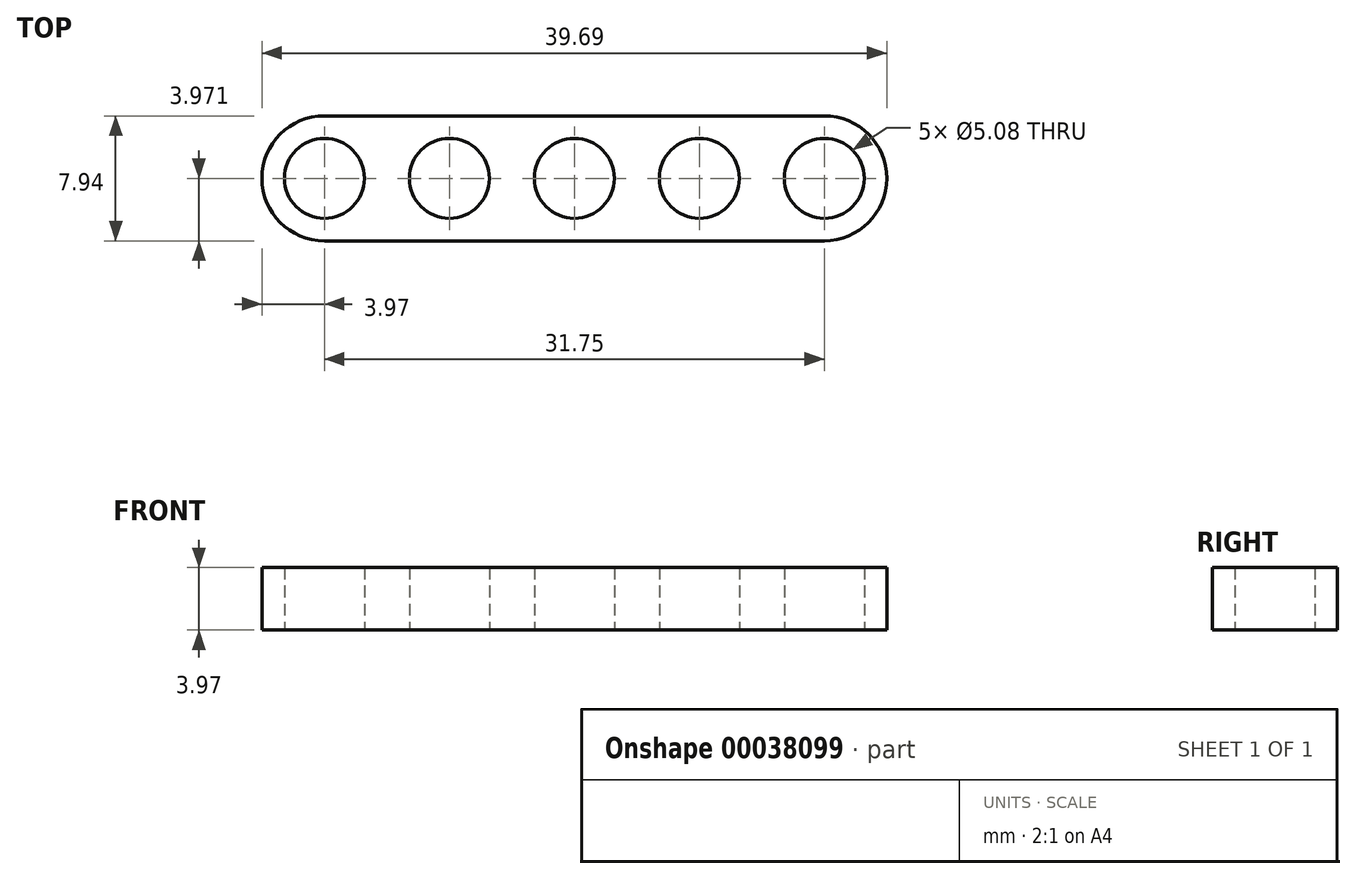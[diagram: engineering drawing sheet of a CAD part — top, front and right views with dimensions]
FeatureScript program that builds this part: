
annotation { "Feature Type Name" : "Feature", "Feature Type Description" : "" }
export const myFeature = defineFeature(function(context is Context, id is Id, definition is map)
    precondition{}
    {
        {
            var Q0;
            Q0=qCreatedBy(makeId("Top.planeOp"),FACE);
            var sketch = newSketch(context, id + "F0", { "sketchPlane" : qUnion([Q0])});
            skLineSegment(sketch, "E0.bottom", {"start": v(0, 0) * mm, "end": v(31.75, 0) * mm});
            skLineSegment(sketch, "E0.top", {"start": v(0, -7.94) * mm, "end": v(31.75, -7.94) * mm});
            skLineSegment(sketch, "E0.left", {"start": v(0, 0) * mm, "end": v(0, -7.94) * mm});
            skLineSegment(sketch, "E0.right", {"start": v(31.75, 0) * mm, "end": v(31.75, -7.94) * mm});
            skLineSegment(sketch, "E1", {"start": v(0, -3.97) * mm, "end": v(7.94, -3.97) * mm, "construction": true});
            skLineSegment(sketch, "E2", {"start": v(7.94, -3.97) * mm, "end": v(15.88, -3.97) * mm, "construction": true});
            skLineSegment(sketch, "E3", {"start": v(15.88, -3.97) * mm, "end": v(23.81, -3.97) * mm, "construction": true});
            skLineSegment(sketch, "E4", {"start": v(23.81, -3.97) * mm, "end": v(31.75, -3.97) * mm, "construction": true});
            skArc(sketch, "E5", {"start": v(0, 0) * mm, "mid": v(-3.97, -3.97) * mm, "end": v(0, -7.94) * mm});
            skArc(sketch, "E6", {"start": v(31.75, -7.94) * mm, "mid": v(35.72, -3.97) * mm, "end": v(31.75, 0) * mm});
            skCircle(sketch, "E7", {"center": v(0, -3.97) * mm, "radius": 2.54 * mm});
            skCircle(sketch, "E8", {"center": v(7.94, -3.97) * mm, "radius": 2.54 * mm});
            skCircle(sketch, "E9", {"center": v(15.88, -3.97) * mm, "radius": 2.54 * mm});
            skCircle(sketch, "E10", {"center": v(23.81, -3.97) * mm, "radius": 2.54 * mm});
            skCircle(sketch, "E11", {"center": v(31.75, -3.97) * mm, "radius": 2.54 * mm});
            skSolve(sketch);
        }
        {
            var Q0;
            Q0=qSketchRegion(id+"F0",true);
            extrude(context, id + "F1", {"entities" : qUnion([Q0]), "depth" : 3.97 * mm});
        }
    });
